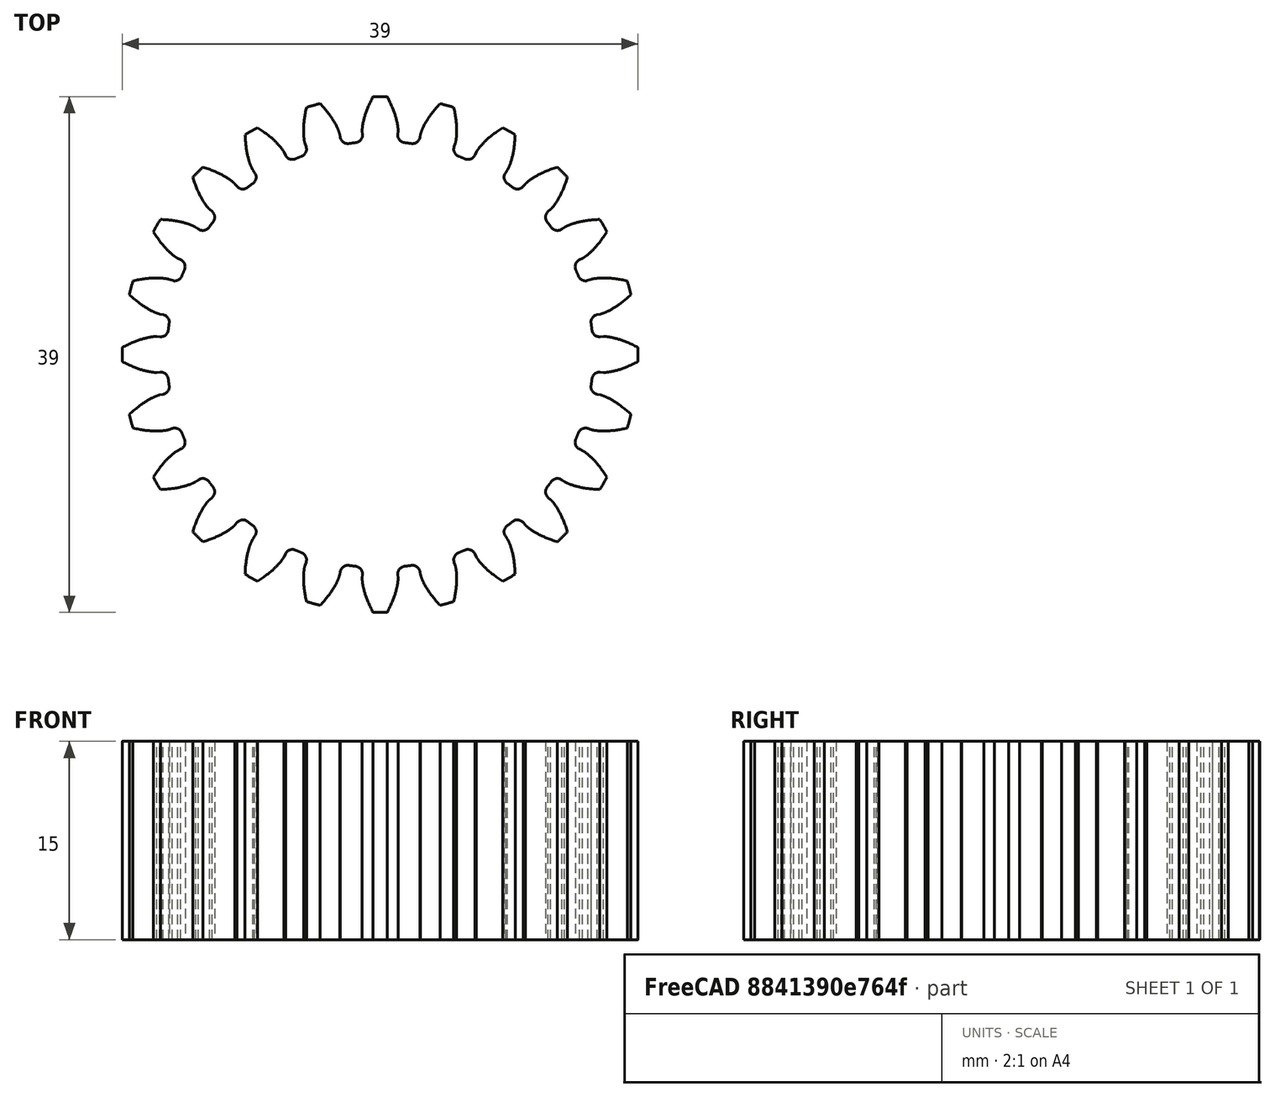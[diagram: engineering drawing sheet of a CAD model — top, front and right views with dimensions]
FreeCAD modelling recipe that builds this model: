
FCSTD DOCUMENT  (FreeCAD 1.0R39319 (Git))
Label: inv gear t24 m1_5 w15
License: All rights reserved
LicenseURL: https://en.wikipedia.org/wiki/All_rights_reserved
objects: Part::Part2DObjectPython×1, PartDesign::Pad×1, PartDesign::Body×1
note: 5 computed .brp shape members not serialized (recipe doc carries the construction recipe); baked Part::Feature solids carry a one-line shape summary decoded from their .brp

FEATURE [Part::Part2DObjectPython] InvoluteGear  # Draft 2D object (typed FeaturePython)
  AddendumCoefficient = 1
  DedendumCoefficient = 1.25
  ExternalGear = true
  HighPrecision = true
  Modules = 1.5
  NumberOfTeeth = 24
  PressureAngle = 20
  ProfileShiftCoefficient = 0
  RootFilletCoefficient = 0.38
FEATURE [PartDesign::Pad] Pad
  Direction = (0,0,1)
  Length = 15
  Length2 = 10
  Profile = -> InvoluteGear
  ReferenceAxis = -> InvoluteGear [N_Axis]
  Refine = true
  Suppressed = false
  Type = 0
FEATURE [PartDesign::Body] Body
  AllowCompound = false
  Group = -> [InvoluteGear,Pad]
  Origin = -> Origin
  Tip = -> Pad
